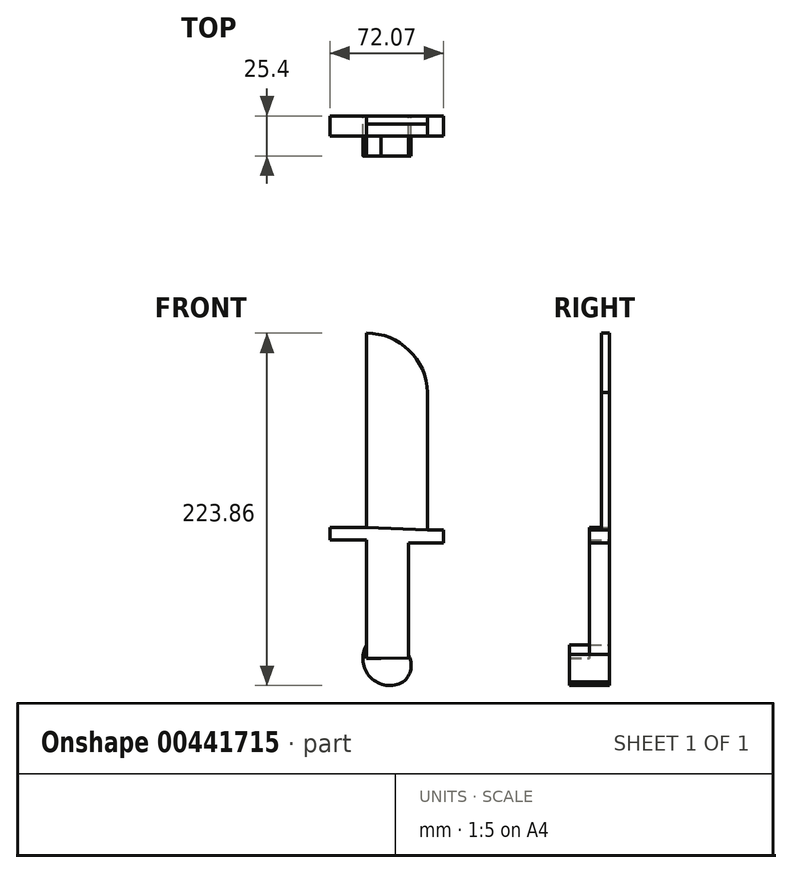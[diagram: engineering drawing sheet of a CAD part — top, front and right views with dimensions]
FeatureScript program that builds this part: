
annotation { "Feature Type Name" : "Feature", "Feature Type Description" : "" }
export const myFeature = defineFeature(function(context is Context, id is Id, definition is map)
    precondition{}
    {
        {
            var Q0;
            Q0=qCreatedBy(makeId("Front.planeOp"),FACE);
            var sketch = newSketch(context, id + "F0", { "sketchPlane" : qUnion([Q0])});
            skLineSegment(sketch, "E0", {"start": v(0, 167.48) * mm, "end": v(0, -103.36) * mm});
            skLineSegment(sketch, "E1", {"start": v(0, -129.94) * mm, "end": v(-9.3, -129.94) * mm});
            skLineSegment(sketch, "E2", {"start": v(-9.3, -129.94) * mm, "end": v(-9.3, -54.55) * mm});
            skLineSegment(sketch, "E3", {"start": v(-9.3, -54.55) * mm, "end": v(-32.46, -54.55) * mm});
            skLineSegment(sketch, "E4", {"start": v(-32.46, -54.55) * mm, "end": v(-32.46, -46.8) * mm});
            skLineSegment(sketch, "E5", {"start": v(-32.46, -46.8) * mm, "end": v(-9.3, -46.8) * mm});
            skLineSegment(sketch, "E6", {"start": v(-9.3, -46.8) * mm, "end": v(-9.3, 37.9) * mm});
            skArc(sketch, "E7", {"start": v(-9.3, 76.73) * mm, "mid": v(17.75, 65.75) * mm, "end": v(29.5, 39.01) * mm});
            skLineSegment(sketch, "E8", {"start": v(-9.3, 37.9) * mm, "end": v(-9.3, 76.73) * mm});
            skLineSegment(sketch, "E9", {"start": v(29.5, 0) * mm, "end": v(29.5, 39.01) * mm});
            skLineSegment(sketch, "E10", {"start": v(29.5, -27.95) * mm, "end": v(29.5, 0) * mm});
            skLineSegment(sketch, "E11", {"start": v(29.5, -48.4) * mm, "end": v(29.5, -27.95) * mm});
            skPoint(sketch, "E11.startSnap0", {"position": v(29.5, -13.98) * mm});
            skLineSegment(sketch, "E12", {"start": v(-9.3, -46.8) * mm, "end": v(29.5, -48.4) * mm});
            skLineSegment(sketch, "E13", {"start": v(39.61, -48.4) * mm, "end": v(29.5, -48.4) * mm});
            skLineSegment(sketch, "E14", {"start": v(39.61, -56.49) * mm, "end": v(39.61, -48.4) * mm});
            skLineSegment(sketch, "E15", {"start": v(39.61, -56.49) * mm, "end": v(29.5, -56.49) * mm});
            skLineSegment(sketch, "E16", {"start": v(29.5, -56.49) * mm, "end": v(17.24, -56.49) * mm});
            skLineSegment(sketch, "E17", {"start": v(17.24, -56.49) * mm, "end": v(17.24, -79.02) * mm});
            skLineSegment(sketch, "E18", {"start": v(17.24, -79.02) * mm, "end": v(17.24, -129.73) * mm});
            skLineSegment(sketch, "E19", {"start": v(17.24, -129.73) * mm, "end": v(0, -129.94) * mm});
            skArc(sketch, "E20", {"start": v(14.01, -144.95) * mm, "mid": v(-6.7, -141.96) * mm, "end": v(-9.3, -121.18) * mm});
            skArc(sketch, "E21", {"start": v(18.48, -144.95) * mm, "mid": v(14.85, -149.34) * mm, "end": v(9.86, -146.6) * mm});
            skArc(sketch, "E22", {"start": v(14.01, -144.95) * mm, "mid": v(18.9, -136.82) * mm, "end": v(17.24, -127.48) * mm});
            skArc(sketch, "E23", {"start": v(18.48, -144.95) * mm, "mid": v(18.1, -143.14) * mm, "end": v(17, -141.64) * mm});
            skSolve(sketch);
        }
        {
            var Q0;
            {var subQ4=sQuery(id+"F0.wireOp",EDGE,"E6");Q0=makeQuery(id+"F0.imprint","IMPRINT",FACE,{"disambiguationData":[TD([[makeQuery(id+"F0.imprint","IMPRINT",EDGE,{"derivedFrom":subQ4}),-1.0]])]});}
            var Q1;
            {var subQ0=sQuery(id+"F0.wireOp",EDGE,"E9");Q1=makeQuery(id+"F0.imprint","IMPRINT",FACE,{"disambiguationData":[TD([[makeQuery(id+"F0.imprint","IMPRINT",EDGE,{"derivedFrom":subQ0}),1.0]])]});}
            extrude(context, id + "F1", {"entities" : qUnion([Q0, Q1]), "depth" : 5.08 * mm});
        }
        {
            var Q0;
            {var subQ2=sQuery(id+"F0.wireOp",EDGE,"E1");Q0=makeQuery(id+"F0.imprint","IMPRINT",FACE,{"disambiguationData":[TD([[makeQuery(id+"F0.imprint","IMPRINT",EDGE,{"derivedFrom":subQ2}),-1.0]])]});}
            extrude(context, id + "F2", {"entities" : qUnion([Q0]), "operationType" : NewBodyOperationType.ADD, "depth" : 12.7 * mm});
        }
        {
            var Q0;
            {var subQ1=sQuery(id+"F0.wireOp",EDGE,"E1");Q0=makeQuery(id+"F0.imprint","IMPRINT",FACE,{"disambiguationData":[TD([[makeQuery(id+"F0.imprint","IMPRINT",EDGE,{"derivedFrom":subQ1}),1.0]])]});}
            var Q1;
            {var subQ3=sQuery(id+"F0.wireOp",EDGE,"E21");Q1=makeQuery(id+"F0.imprint","IMPRINT",FACE,{"disambiguationData":[TD([[makeQuery(id+"F0.imprint","IMPRINT",EDGE,{"derivedFrom":subQ3}),-1.0]])]});}
            extrude(context, id + "F3", {"entities" : qUnion([Q0, Q1]), "operationType" : NewBodyOperationType.ADD, "depth" : 25.4 * mm});
        }
    });
